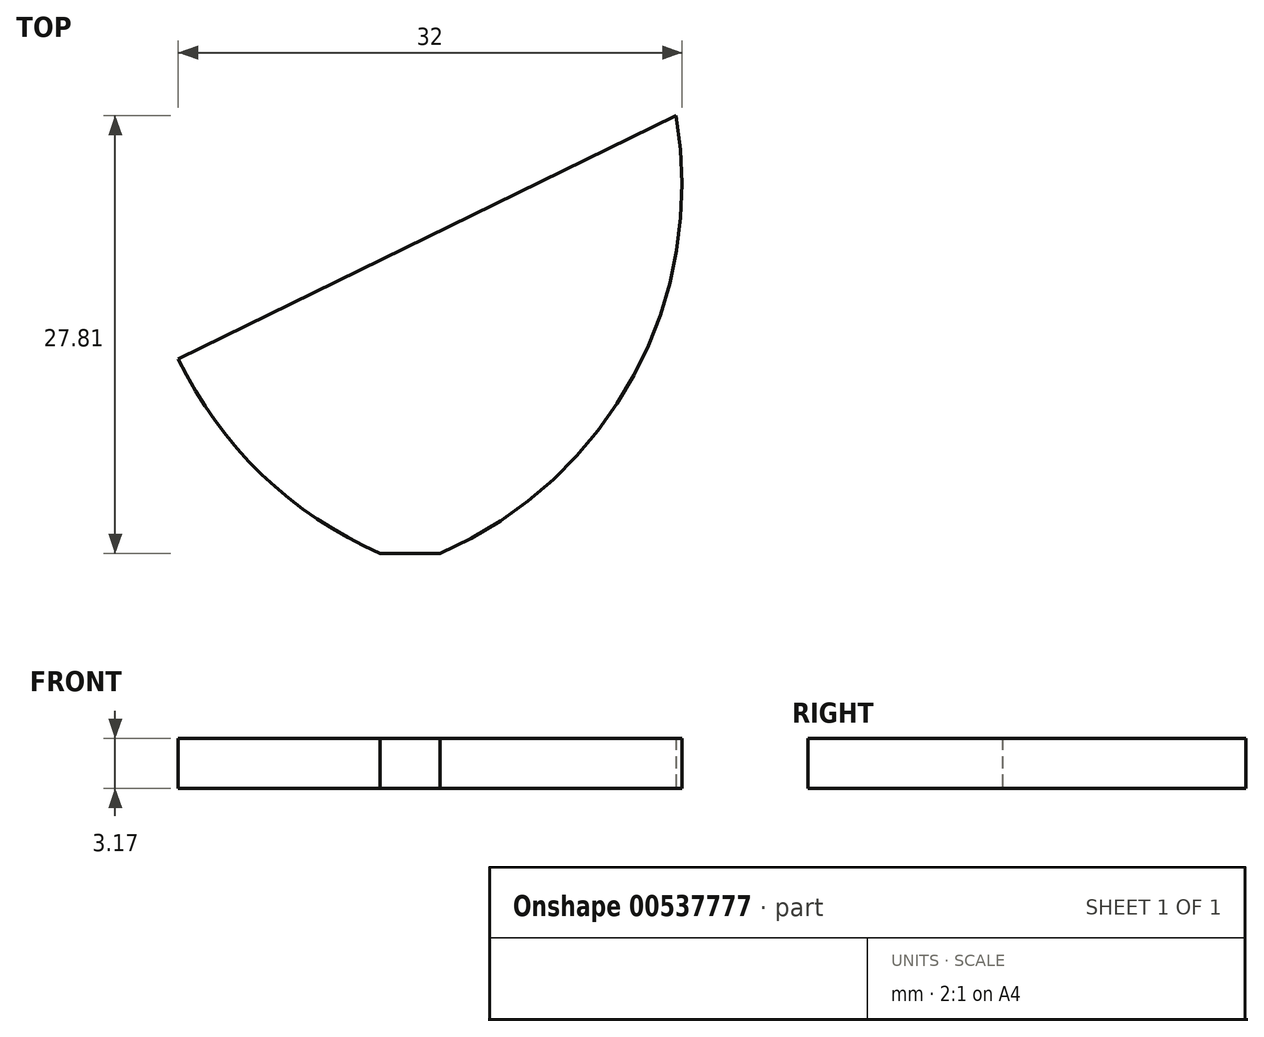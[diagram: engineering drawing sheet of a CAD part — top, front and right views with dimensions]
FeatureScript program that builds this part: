
annotation { "Feature Type Name" : "Feature", "Feature Type Description" : "" }
export const myFeature = defineFeature(function(context is Context, id is Id, definition is map)
    precondition{}
    {
        {
            var Q0;
            Q0=qCreatedBy(makeId("Top.planeOp"),FACE);
            var sketch = newSketch(context, id + "F0", { "sketchPlane" : qUnion([Q0])});
            skPoint(sketch, "E0.middle", {"position": v(1.8, -5.3) * mm});
            skArc(sketch, "E1", {"start": v(-12.93, 7.03) * mm, "mid": v(-7.62, -0.3) * mm, "end": v(-0.1, -5.3) * mm});
            skArc(sketch, "E2.MirrorCS", {"start": v(18.69, 22.5) * mm, "mid": v(16, 6) * mm, "end": v(3.7, -5.3) * mm});
            skPoint(sketch, "E3.orphan", {"position": v(-0.1, -37.06) * mm});
            skPoint(sketch, "E4.orphan", {"position": v(-0.1, 26.44) * mm});
            skLineSegment(sketch, "E5", {"start": v(-0.1, -5.3) * mm, "end": v(3.7, -5.3) * mm});
            skPoint(sketch, "E6.orphan", {"position": v(-17.25, 26.44) * mm});
            skPoint(sketch, "E0.top.end.orphan", {"position": v(17.68, 26.44) * mm});
            skLineSegment(sketch, "E7", {"start": v(-12.93, 7.03) * mm, "end": v(18.69, 22.5) * mm});
            skSolve(sketch);
        }
        {
            var Q0;
            Q0=makeQuery(id+"F0.imprint","IMPRINT",FACE,{"disambiguationData":[TD([[makeQuery(id+"F0.imprint","IMPRINT",EDGE,{"derivedFrom":sQuery(id+"F0.wireOp",EDGE,"E1")}),1.0]])]});
            extrude(context, id + "F1", {"entities" : qUnion([Q0]), "depth" : 3.17 * mm, "offsetDistance" : 25.4 * mm});
        }
    });
